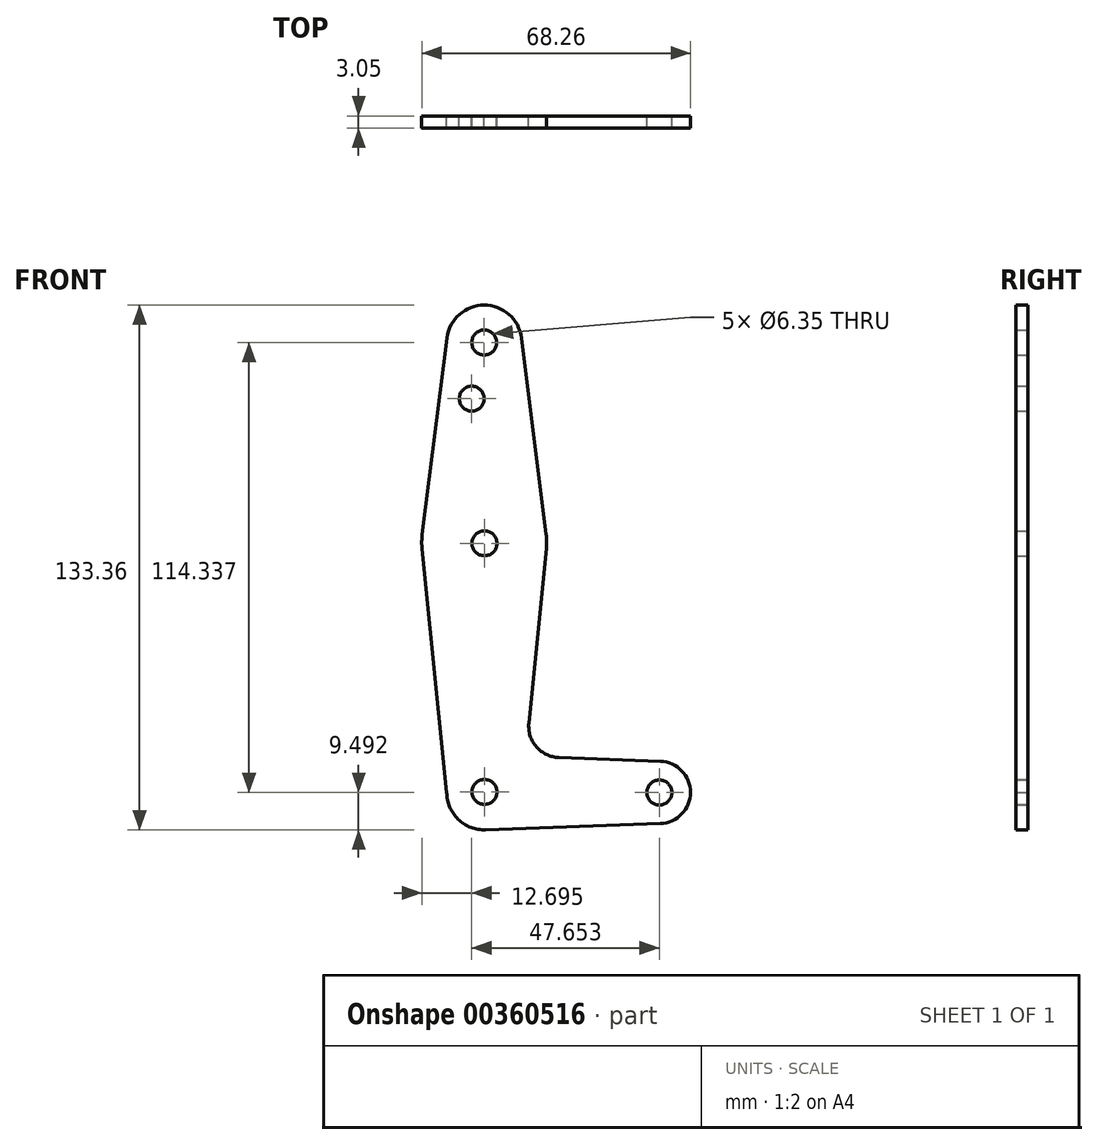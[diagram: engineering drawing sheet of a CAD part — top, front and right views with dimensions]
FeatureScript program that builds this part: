
annotation { "Feature Type Name" : "Feature", "Feature Type Description" : "" }
export const myFeature = defineFeature(function(context is Context, id is Id, definition is map)
    precondition{}
    {
        {
            var Q0;
            Q0=qCreatedBy(makeId("Front.planeOp"),FACE);
            var sketch = newSketch(context, id + "F0", { "sketchPlane" : qUnion([Q0])});
            skLineSegment(sketch, "E0", {"start": v(0, 114.3) * mm, "end": v(0, 0) * mm, "construction": true});
            skLineSegment(sketch, "E1", {"start": v(0, 0) * mm, "end": v(44.45, 0) * mm, "construction": true});
            skCircle(sketch, "E2", {"center": v(0, 114.3) * mm, "radius": 9.53 * mm});
            skCircle(sketch, "E3", {"center": v(0, 63.5) * mm, "radius": 15.88 * mm});
            skCircle(sketch, "E4", {"center": v(0, 0) * mm, "radius": 9.53 * mm});
            skCircle(sketch, "E5", {"center": v(44.45, 0) * mm, "radius": 7.94 * mm});
            skLineSegment(sketch, "E6", {"start": v(-15.75, 65.48) * mm, "end": v(-9.45, 115.5) * mm});
            skLineSegment(sketch, "E7", {"start": v(15.75, 65.48) * mm, "end": v(9.45, 115.5) * mm});
            skLineSegment(sketch, "E8", {"start": v(-9.52, 0) * mm, "end": v(-15.8, 61.9) * mm});
            skLineSegment(sketch, "E9", {"start": v(11.34, 17.6) * mm, "end": v(15.8, 61.91) * mm});
            skLineSegment(sketch, "E10", {"start": v(0.34, -9.52) * mm, "end": v(44.73, -7.93) * mm});
            skLineSegment(sketch, "E11", {"start": v(44.73, 7.93) * mm, "end": v(18.97, 8.85) * mm});
            skCircle(sketch, "E12", {"center": v(0, 114.3) * mm, "radius": 3.18 * mm});
            skCircle(sketch, "E13", {"center": v(0.05, 63.29) * mm, "radius": 3.18 * mm});
            skCircle(sketch, "E14", {"center": v(0.05, 0.12) * mm, "radius": 3.18 * mm});
            skCircle(sketch, "E15", {"center": v(44.48, -0.04) * mm, "radius": 3.18 * mm});
            skCircle(sketch, "E16", {"center": v(-3.17, 100.03) * mm, "radius": 3.18 * mm});
            skArc(sketch, "E17.filletArc", {"start": v(11.34, 17.6) * mm, "mid": v(13.26, 11.57) * mm, "end": v(18.97, 8.85) * mm});
            skSolve(sketch);
        }
        {
            var Q0;
            Q0 = qSketchRegion(id + "F0", true);
            extrude(context, id + "F1", {"entities" : qUnion([Q0]), "depth" : 3.05 * mm});
        }
    });
